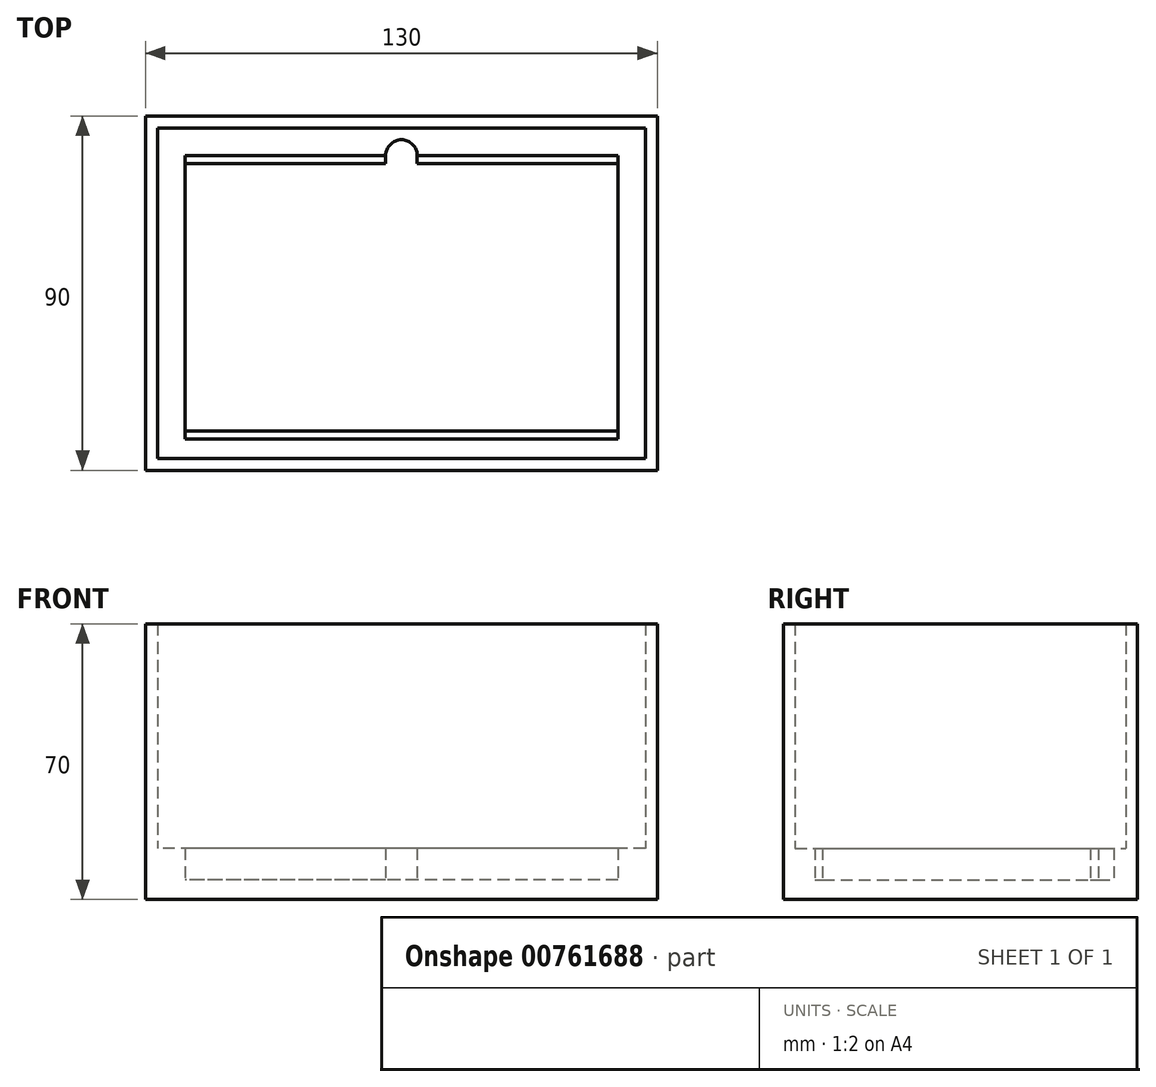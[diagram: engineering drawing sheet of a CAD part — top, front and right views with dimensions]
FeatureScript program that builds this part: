
annotation { "Feature Type Name" : "Feature", "Feature Type Description" : "" }
export const myFeature = defineFeature(function(context is Context, id is Id, definition is map)
    precondition{}
    {
        {
            var Q0;
            Q0=qCreatedBy(makeId("Top.planeOp"),FACE);
            var sketch = newSketch(context, id + "F0", { "sketchPlane" : qUnion([Q0])});
            skLineSegment(sketch, "E0.bottom", {"start": v(54.95, -34.86) * mm, "end": v(-55.05, -34.86) * mm});
            skLineSegment(sketch, "E0.top", {"start": v(54.95, 35.14) * mm, "end": v(-55.05, 35.14) * mm});
            skLineSegment(sketch, "E0.left", {"start": v(54.95, -34.86) * mm, "end": v(54.95, 35.14) * mm});
            skLineSegment(sketch, "E0.right", {"start": v(-55.05, -34.86) * mm, "end": v(-55.05, 35.14) * mm});
            skPoint(sketch, "E0.middle", {"position": v(-0.05, 0.14) * mm});
            skLineSegment(sketch, "E1.0", {"start": v(-62.05, -41.86) * mm, "end": v(-62.05, 42.14) * mm});
            skLineSegment(sketch, "E1.1", {"start": v(61.95, -41.86) * mm, "end": v(-62.05, -41.86) * mm});
            skLineSegment(sketch, "E1.2", {"start": v(61.95, -41.86) * mm, "end": v(61.95, 42.14) * mm});
            skLineSegment(sketch, "E1.3", {"start": v(61.95, 42.14) * mm, "end": v(-62.05, 42.14) * mm});
            skLineSegment(sketch, "E2.0", {"start": v(-65.05, -44.86) * mm, "end": v(-65.05, 45.14) * mm});
            skLineSegment(sketch, "E2.1", {"start": v(64.95, -44.86) * mm, "end": v(-65.05, -44.86) * mm});
            skLineSegment(sketch, "E2.2", {"start": v(64.95, -44.86) * mm, "end": v(64.95, 45.14) * mm});
            skLineSegment(sketch, "E2.3", {"start": v(64.95, 45.14) * mm, "end": v(-65.05, 45.14) * mm});
            skLineSegment(sketch, "E3", {"start": v(-0.05, 35.14) * mm, "end": v(0, 42.14) * mm});
            skLineSegment(sketch, "E4", {"start": v(-0.05, 35.14) * mm, "end": v(-4.05, 35.14) * mm});
            skLineSegment(sketch, "E5", {"start": v(-0.05, 35.14) * mm, "end": v(3.95, 35.14) * mm});
            skArc(sketch, "E6", {"start": v(3.95, 35.14) * mm, "mid": v(-0.05, 39.14) * mm, "end": v(-4.05, 35.14) * mm});
            skSolve(sketch);
        }
        {
            var Q0;
            {var subQ1=sQuery(id+"F0.wireOp",EDGE,"E1.0");Q0=makeQuery(id+"F0.imprint","IMPRINT",FACE,{"disambiguationData":[TD([[makeQuery(id+"F0.imprint","IMPRINT",EDGE,{"derivedFrom":subQ1}),1.0]])]});}
            extrude(context, id + "F1", {"entities" : qUnion([Q0]), "depth" : 70 * mm, "offsetDistance" : 25 * mm});
        }
        {
            var Q0;
            Q0=makeQuery(id+"F0.imprint","IMPRINT",FACE,{"disambiguationData":[TD([[makeQuery(id+"F0.imprint","IMPRINT",EDGE,{"derivedFrom":sQuery(id+"F0.wireOp",EDGE,"E0.bottom")}),1.0]])]});
            extrude(context, id + "F2", {"entities" : qUnion([Q0]), "operationType" : NewBodyOperationType.ADD, "depth" : 13 * mm, "offsetDistance" : 25 * mm});
        }
        {
            var Q0;
            Q0=makeQuery(id+"F0.imprint","IMPRINT",FACE,{"disambiguationData":[TD([[makeQuery(id+"F0.imprint","IMPRINT",EDGE,{"derivedFrom":sQuery(id+"F0.wireOp",EDGE,"E0.bottom")}),-1.0]])]});
            var Q1;
            {var subQ0=sQuery(id+"F0.wireOp",EDGE,"E3");var subQ1=sQuery(id+"F0.wireOp",EDGE,"E0.top");var subQ2=makeQuery(id+"F0.imprint","INTERSECT",VERTEX,{"derivedFrom":[subQ1,subQ0]});Q1=makeQuery(id+"F0.imprint","IMPRINT",FACE,{"disambiguationData":[TD([[makeQuery(id+"F0.imprint","IMPRINT",EDGE,{"disambiguationData":[TD([[subQ2,-1.0]])],"derivedFrom":subQ1}),-1.0]])]});}
            var Q2;
            {var subQ0=sQuery(id+"F0.wireOp",EDGE,"E3");var subQ1=sQuery(id+"F0.wireOp",EDGE,"E0.top");var subQ2=makeQuery(id+"F0.imprint","INTERSECT",VERTEX,{"derivedFrom":[subQ1,subQ0]});Q2=makeQuery(id+"F0.imprint","IMPRINT",FACE,{"disambiguationData":[TD([[makeQuery(id+"F0.imprint","IMPRINT",EDGE,{"disambiguationData":[TD([[subQ2,1.0]])],"derivedFrom":subQ1}),-1.0]])]});}
            extrude(context, id + "F3", {"entities" : qUnion([Q0, Q1, Q2]), "operationType" : NewBodyOperationType.ADD, "depth" : 5 * mm, "offsetDistance" : 25 * mm});
        }
        {
            var Q0;
            {var subQ0=sQuery(id+"F0.wireOp",EDGE,"E0.top");Q0=makeQuery(id+"F2.opExtrude","SWEPT_FACE",FACE,{"disambiguationData":[OSD([subQ0]),TDD([makeQuery(id+"F0.imprint","IMPRINT",EDGE,{"disambiguationData":[TD([[makeQuery(id+"F0.imprint","INTERSECT",VERTEX,{"derivedFrom":[subQ0,sQuery(id+"F0.wireOp",EDGE,"E0.right")]}),1.0]])],"derivedFrom":subQ0})])]});}
            var Q1;
            Q1=makeQuery(id+"F2.opExtrude","SWEPT_FACE",FACE,{"disambiguationData":[OSD([sQuery(id+"F0.wireOp",EDGE,"E0.bottom")])]});
            var Q2;
            {var subQ0=sQuery(id+"F0.wireOp",EDGE,"E0.top");Q2=makeQuery(id+"F2.opExtrude","SWEPT_FACE",FACE,{"disambiguationData":[OSD([subQ0]),TDD([makeQuery(id+"F0.imprint","IMPRINT",EDGE,{"disambiguationData":[TD([[makeQuery(id+"F0.imprint","INTERSECT",VERTEX,{"derivedFrom":[subQ0,sQuery(id+"F0.wireOp",EDGE,"E0.left")]}),-1.0]])],"derivedFrom":subQ0})])]});}
            extrude(context, id + "F4", {"entities" : qUnion([Q0, Q1, Q2]), "depth" : 2 * mm, "offsetDistance" : 25 * mm});
        }
    });
